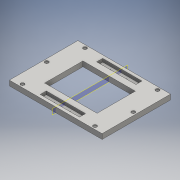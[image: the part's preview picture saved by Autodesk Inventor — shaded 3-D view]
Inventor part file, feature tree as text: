
AUTODESK INVENTOR PART (.ipt)
format: ipt  version: 2016 (Build 200138000, 138)  size: 163,840 bytes
history: native  units: mm
features: sketch x4, mirror x3, extrude x2, hole x2, plane x1
ambient origin geometry x8: Origin, YZ Plane, XZ Plane, XY Plane, X Axis, Y Axis, Z Axis, Center Point
bodies: Solid1 (feature_tree)
feature tree (12):
  extrude  "Extrusion1"  Depth=340.0mm
  extrude  "Extrusion2"  Depth=230.0mm
  hole  "Hole1"  [1 undecoded]
  mirror  "Mirror2"
  hole  "Hole2"  [1 undecoded]
  mirror  "Mirror3"
  mirror  "Mirror4"
  sketch  "Sketch1"  dims[d0=460.0mm d1=340.0mm]
  sketch  "Sketch2"  dims[d2=170.0mm d3=230.0mm]
  sketch  "Sketch3"  dims[d4=100.0mm d5=100.0mm]
  sketch  "Sketch4"  dims[d6=75.0mm d7=75.0mm d8=25.0mm d9=0.0mm d10=30.0mm d11=195.0mm d12=15.0mm d13=16.0mm d14=0.0mm d15=15.0mm d16=80.0mm d17=40.0mm d18=5.5mm d19=6.0mm d20=4.0mm d21=2.0mm d22=90.0deg d23=8.0mm d24=20.594885mm d25=15.0mm d26=15.0mm d27=50.0mm d28=6.6mm d29=6.0mm d30=18.0mm d31=6.6mm d32=90.0deg d33=8.0mm d34=20.594885mm]
  plane  "Work Plane1"
note: 2 required parameter values undecoded (feature->parameter linkage not recoverable at this tier; creation-order binding heuristic only, values carry confidence <= 0.55)
